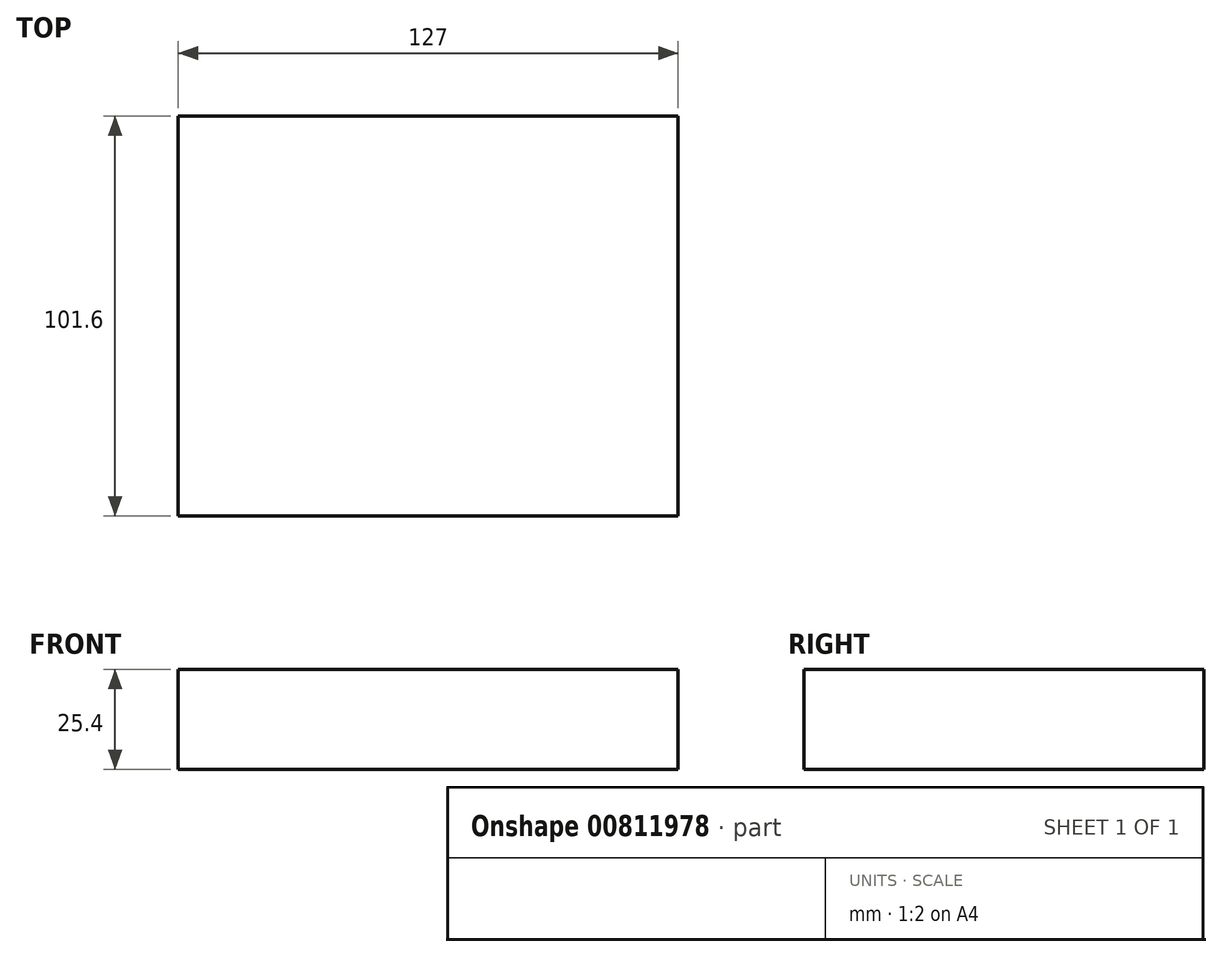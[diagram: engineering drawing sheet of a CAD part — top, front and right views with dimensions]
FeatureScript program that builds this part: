
annotation { "Feature Type Name" : "Feature", "Feature Type Description" : "" }
export const myFeature = defineFeature(function(context is Context, id is Id, definition is map)
    precondition{}
    {
        {
            var Q0;
            Q0=qCreatedBy(makeId("Top.planeOp"),FACE);
            var sketch = newSketch(context, id + "F0", { "sketchPlane" : qUnion([Q0])});
            skLineSegment(sketch, "E0.bottom", {"start": v(-56.36, 53.08) * mm, "end": v(70.64, 53.08) * mm});
            skLineSegment(sketch, "E0.top", {"start": v(-56.36, -48.52) * mm, "end": v(70.64, -48.52) * mm});
            skLineSegment(sketch, "E0.left", {"start": v(-56.36, 53.08) * mm, "end": v(-56.36, -48.52) * mm});
            skLineSegment(sketch, "E0.right", {"start": v(70.64, 53.08) * mm, "end": v(70.64, -48.52) * mm});
            skSolve(sketch);
        }
        {
            var Q0;
            Q0=makeQuery(id+"F0.imprint","IMPRINT",FACE,{"disambiguationData":[TD([[makeQuery(id+"F0.imprint","IMPRINT",EDGE,{"derivedFrom":sQuery(id+"F0.wireOp",EDGE,"E0.bottom")}),-1.0]])]});
            extrude(context, id + "F1", {"entities" : qUnion([Q0]), "depth" : 25.4 * mm, "offsetDistance" : 25.4 * mm});
        }
    });
